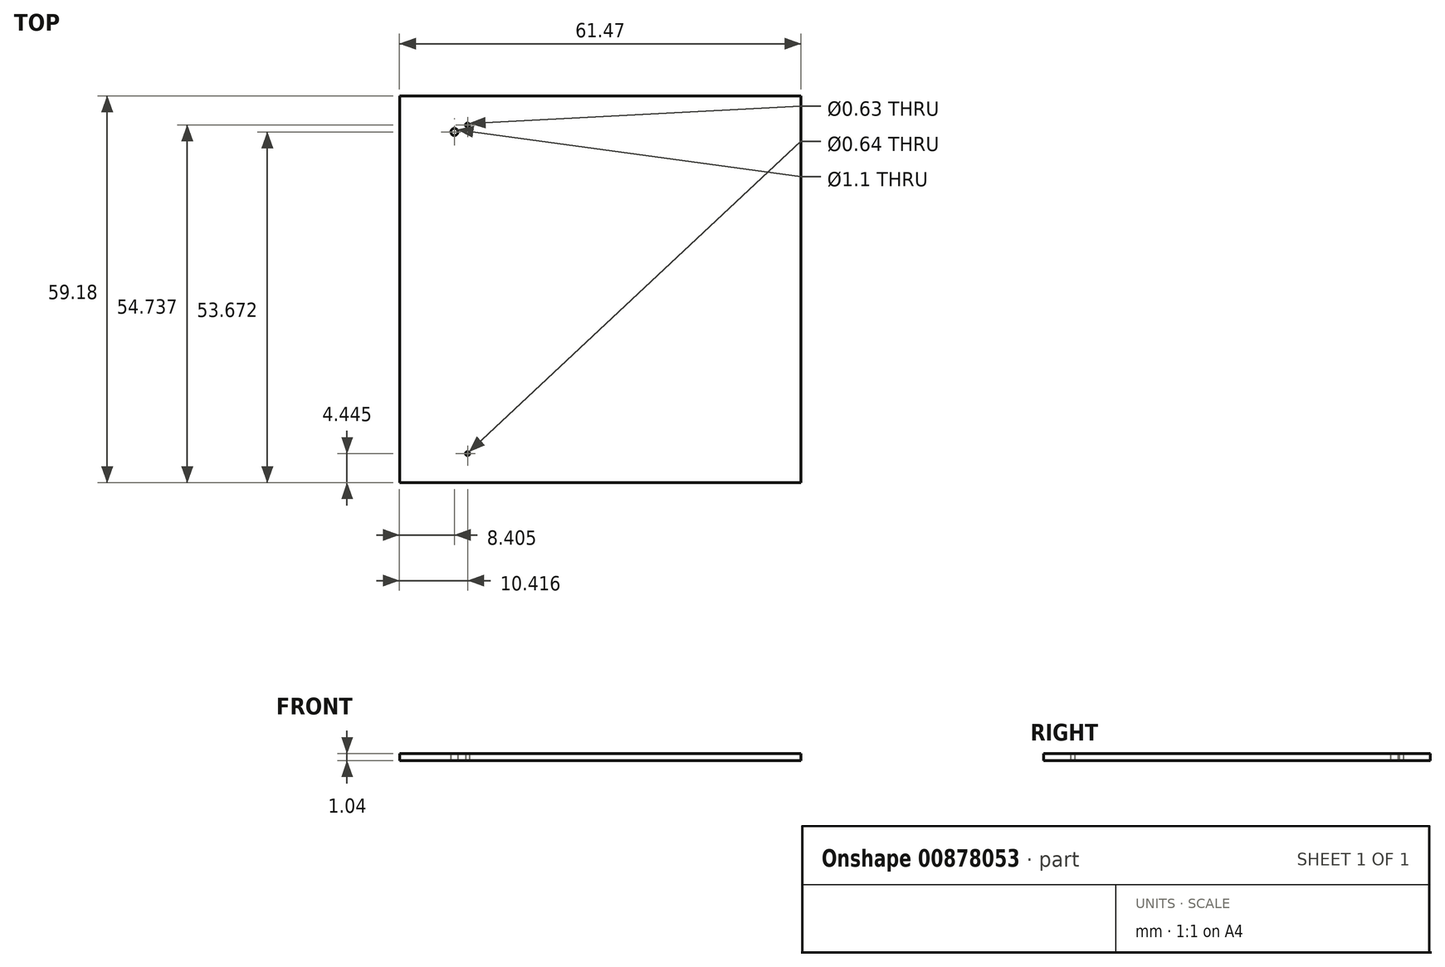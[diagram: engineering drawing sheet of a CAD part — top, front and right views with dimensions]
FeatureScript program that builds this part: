
annotation { "Feature Type Name" : "Feature", "Feature Type Description" : "" }
export const myFeature = defineFeature(function(context is Context, id is Id, definition is map)
    precondition{}
    {
        {
            var Q0;
            Q0=qCreatedBy(makeId("Top.planeOp"),FACE);
            var sketch = newSketch(context, id + "F0", { "sketchPlane" : qUnion([Q0])});
            skLineSegment(sketch, "E0.bottom", {"start": v(0, 0) * mm, "end": v(-61.47, 0) * mm});
            skLineSegment(sketch, "E0.top", {"start": v(0, 59.18) * mm, "end": v(-61.47, 59.18) * mm});
            skLineSegment(sketch, "E0.left", {"start": v(0, 0) * mm, "end": v(0, 59.18) * mm});
            skLineSegment(sketch, "E0.right", {"start": v(-61.47, 0) * mm, "end": v(-61.47, 59.18) * mm});
            skLineSegment(sketch, "E1", {"start": v(-51.05, 0) * mm, "end": v(-51.05, 4.44) * mm});
            skCircle(sketch, "E2", {"center": v(-51.05, 4.44) * mm, "radius": 0.32 * mm});
            skLineSegment(sketch, "E3", {"start": v(-51.05, 4.44) * mm, "end": v(-51.05, 54.74) * mm});
            skCircle(sketch, "E4", {"center": v(-51.05, 54.74) * mm, "radius": 0.32 * mm});
            skLineSegment(sketch, "E5", {"start": v(-51.05, 54.74) * mm, "end": v(-61.47, 54.74) * mm});
            skCircle(sketch, "E6", {"center": v(-53.06, 53.67) * mm, "radius": 0.55 * mm});
            skSolve(sketch);
        }
        {
            var Q0;
            Q0=makeQuery(id+"F0.imprint","IMPRINT",FACE,{"disambiguationData":[TD([[makeQuery(id+"F0.imprint","IMPRINT",EDGE,{"derivedFrom":sQuery(id+"F0.wireOp",EDGE,"E0.bottom")}),-1.0]])]});
            var Q1;
            {var subQ6=sQuery(id+"F0.wireOp",EDGE,"E0.top");Q1=makeQuery(id+"F0.imprint","IMPRINT",FACE,{"disambiguationData":[TD([[makeQuery(id+"F0.imprint","IMPRINT",EDGE,{"derivedFrom":subQ6}),1.0]])]});}
            extrude(context, id + "F1", {"entities" : qUnion([Q0, Q1]), "depth" : 1.04 * mm, "offsetDistance" : 25.4 * mm});
        }
    });
